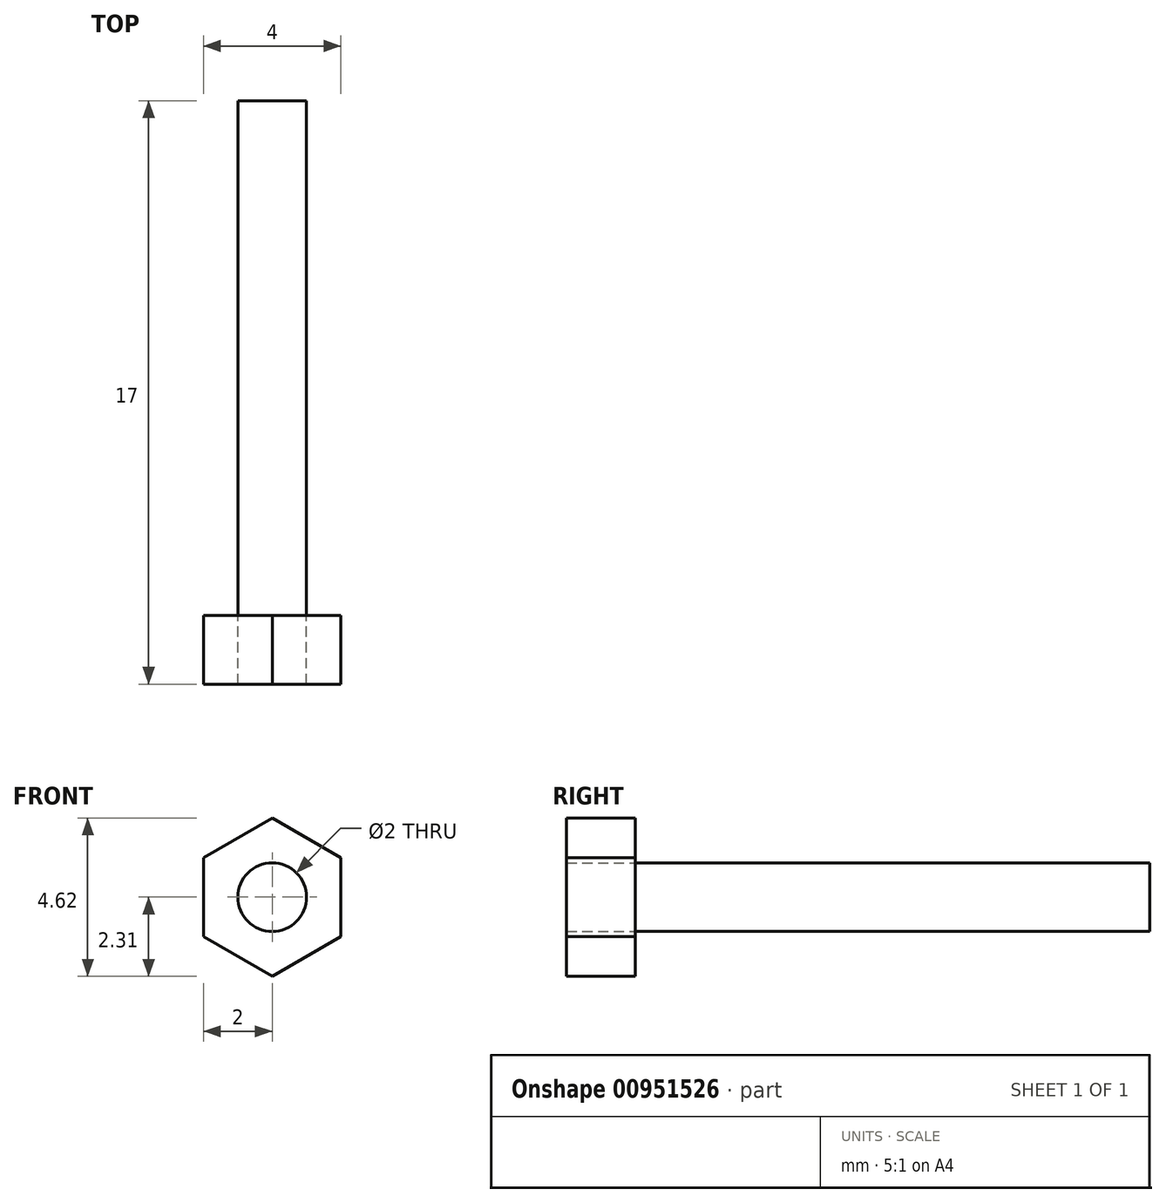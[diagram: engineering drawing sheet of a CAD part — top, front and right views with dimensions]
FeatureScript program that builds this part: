
annotation { "Feature Type Name" : "Feature", "Feature Type Description" : "" }
export const myFeature = defineFeature(function(context is Context, id is Id, definition is map)
    precondition{}
    {
        {
            var Q0;
            Q0=qCreatedBy(makeId("Front.planeOp"),FACE);
            var sketch = newSketch(context, id + "F0", { "sketchPlane" : qUnion([Q0])});
            skCircle(sketch, "E0", {"center": v(0, 0) * mm, "radius": 1 * mm});
            skCircle(sketch, "E1.cCircle", {"center": v(0, 0) * mm, "radius": 2 * mm, "construction": true});
            skLineSegment(sketch, "E1.0", {"start": v(-2, -1.15) * mm, "end": v(-2, 1.15) * mm});
            skLineSegment(sketch, "E1.1", {"start": v(-2, 1.15) * mm, "end": v(0, 2.3) * mm});
            skLineSegment(sketch, "E1.2", {"start": v(0, 2.3) * mm, "end": v(2, 1.15) * mm});
            skLineSegment(sketch, "E1.3", {"start": v(2, 1.15) * mm, "end": v(2, -1.15) * mm});
            skLineSegment(sketch, "E1.4", {"start": v(2, -1.15) * mm, "end": v(0, -2.3) * mm});
            skLineSegment(sketch, "E1.5", {"start": v(0, -2.3) * mm, "end": v(-2, -1.15) * mm});
            skPoint(sketch, "E1.0.midPoint", {"position": v(-2, 0) * mm});
            skSolve(sketch);
        }
        {
            var Q0;
            Q0=qSketchRegion(id+"F0",true);
            var Q1;
            Q1=makeQuery(id+"F0.imprint","IMPRINT",FACE,{"disambiguationData":[TD([[makeQuery(id+"F0.imprint","IMPRINT",EDGE,{"derivedFrom":sQuery(id+"F0.wireOp",EDGE,"E0")}),1.0]])]});
            extrude(context, id + "F1", {"entities" : qUnion([Q0, Q1]), "depth" : 2 * mm, "offsetDistance" : 25 * mm});
        }
        {
            var Q0;
            Q0=makeQuery(id+"F1.opExtrude","CAP_FACE",FACE,{"disambiguationData":[OSD([sQuery(id+"F0.wireOp",EDGE,"E1.0"),sQuery(id+"F0.wireOp",EDGE,"E1.1"),sQuery(id+"F0.wireOp",EDGE,"E1.2"),sQuery(id+"F0.wireOp",EDGE,"E1.3"),sQuery(id+"F0.wireOp",EDGE,"E1.4"),sQuery(id+"F0.wireOp",EDGE,"E1.5")])],"isStart":true});
            var sketch = newSketch(context, id + "F2", { "sketchPlane" : qUnion([Q0])});
            skCircle(sketch, "E2", {"center": v(0, 0) * mm, "radius": 1 * mm});
            skSolve(sketch);
        }
        {
            var Q0;
            Q0=qSketchRegion(id+"F2",true);
            extrude(context, id + "F3", {"entities" : qUnion([Q0]), "operationType" : NewBodyOperationType.ADD, "depth" : 15 * mm, "offsetDistance" : 25 * mm});
        }
        {
            var Q0;
            Q0=qSketchRegion(id+"F2",true);
            extrude(context, id + "F4", {"entities" : qUnion([Q0]), "operationType" : NewBodyOperationType.ADD, "depth" : 10 * mm, "offsetDistance" : 25 * mm});
        }
        {
            var Q0;
            Q0=makeQuery(id+"F0.imprint","IMPRINT",FACE,{"disambiguationData":[TD([[makeQuery(id+"F0.imprint","IMPRINT",EDGE,{"derivedFrom":sQuery(id+"F0.wireOp",EDGE,"E0")}),-1.0]])]});
            extrude(context, id + "F5", {"entities" : qUnion([Q0]), "depth" : 2 * mm, "offsetDistance" : 25 * mm});
        }
    });
